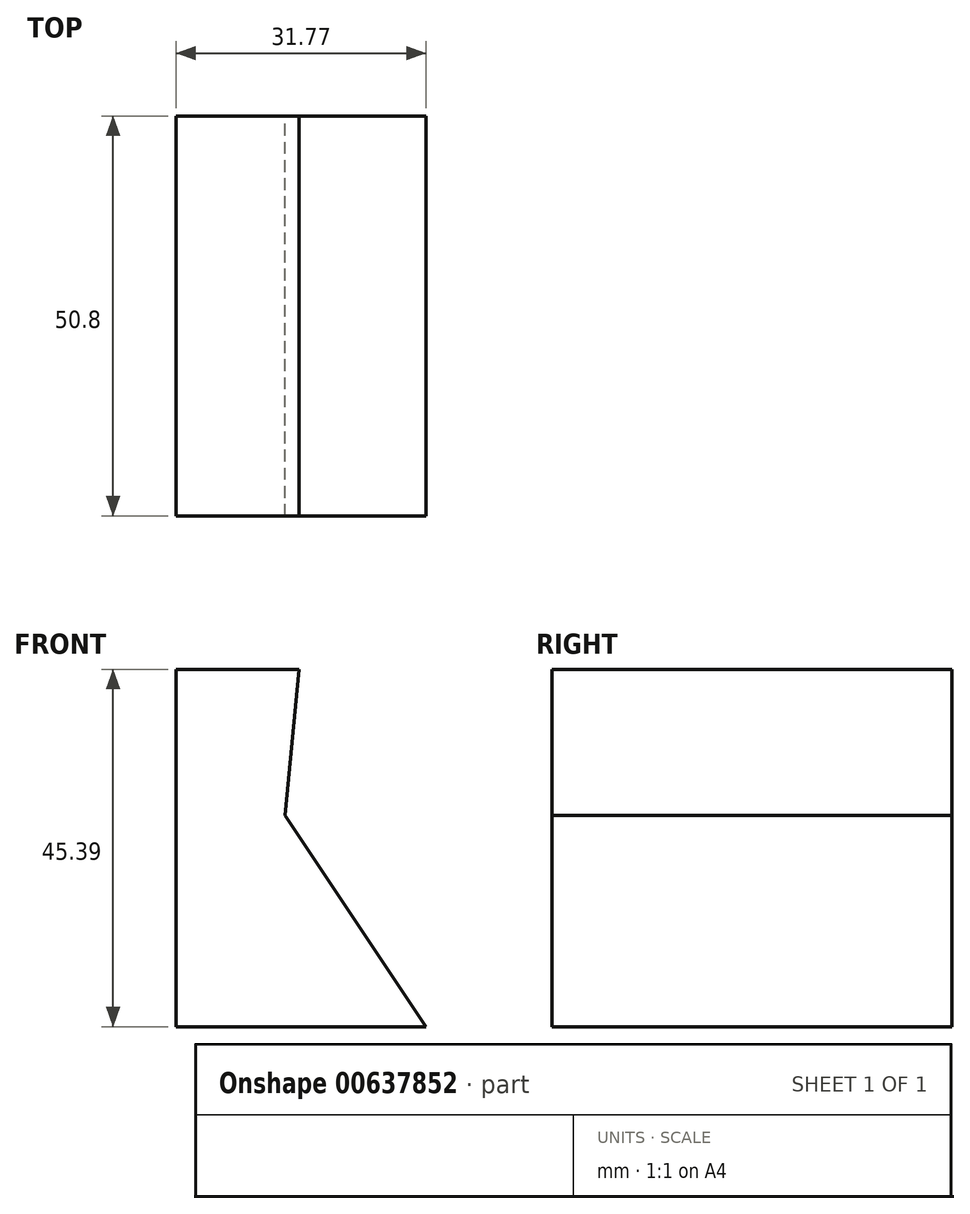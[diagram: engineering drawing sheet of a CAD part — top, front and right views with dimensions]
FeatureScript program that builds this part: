
annotation { "Feature Type Name" : "Feature", "Feature Type Description" : "" }
export const myFeature = defineFeature(function(context is Context, id is Id, definition is map)
    precondition{}
    {
        {
            var Q0;
            Q0=qCreatedBy(makeId("Front.planeOp"),FACE);
            var sketch = newSketch(context, id + "F0", { "sketchPlane" : qUnion([Q0])});
            skLineSegment(sketch, "E0", {"start": v(-71.53, 59) * mm, "end": v(-71.53, 13.61) * mm});
            skLineSegment(sketch, "E1", {"start": v(-71.53, 13.61) * mm, "end": v(-39.76, 13.61) * mm});
            skLineSegment(sketch, "E2", {"start": v(-71.53, 59) * mm, "end": v(-55.94, 59) * mm});
            skLineSegment(sketch, "E3", {"start": v(-55.94, 59) * mm, "end": v(-57.71, 40.45) * mm});
            skLineSegment(sketch, "E4", {"start": v(-57.71, 40.45) * mm, "end": v(-39.76, 13.61) * mm});
            skSolve(sketch);
        }
        {
            var Q0;
            Q0 = qSketchRegion(id + "F0", true);
            extrude(context, id + "F1", {"entities" : qUnion([Q0]), "depth" : 50.8 * mm, "offsetDistance" : 25.4 * mm});
        }
    });
